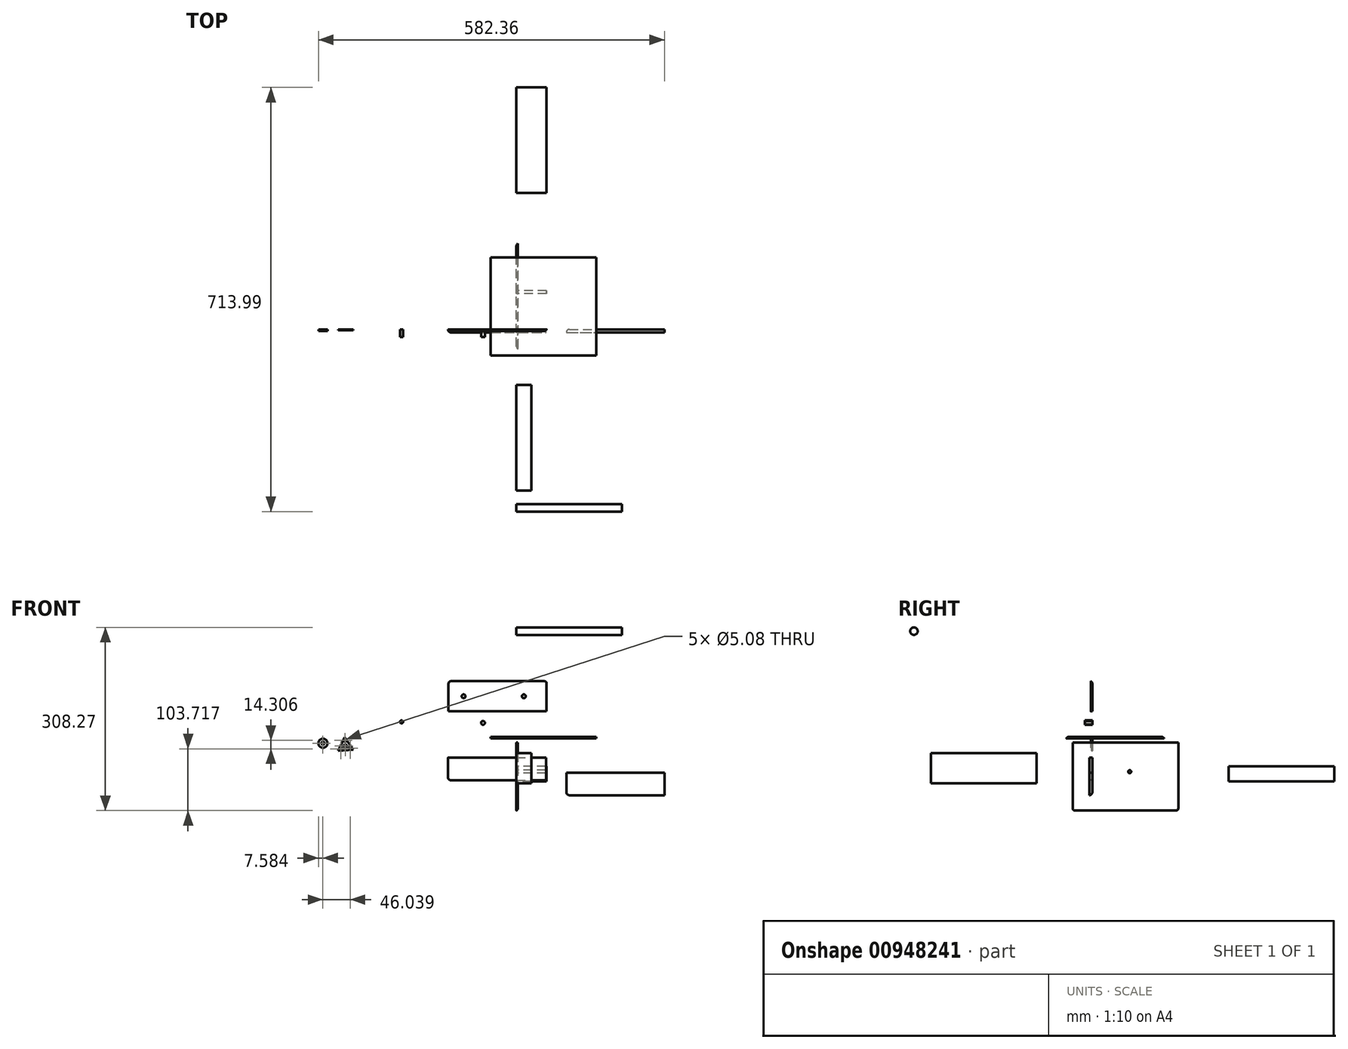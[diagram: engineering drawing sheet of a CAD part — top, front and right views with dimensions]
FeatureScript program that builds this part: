
annotation { "Feature Type Name" : "Feature", "Feature Type Description" : "" }
export const myFeature = defineFeature(function(context is Context, id is Id, definition is map)
    precondition{}
    {
        {
            var Q0;
            Q0=qCreatedBy(makeId("Top.planeOp"),FACE);
            var sketch = newSketch(context, id + "F0", { "sketchPlane" : qUnion([Q0])});
            skLineSegment(sketch, "E0.bottom", {"start": v(-43.18, -44.05) * mm, "end": v(134.62, -44.05) * mm});
            skLineSegment(sketch, "E0.top", {"start": v(-43.18, 121.05) * mm, "end": v(134.62, 121.05) * mm});
            skLineSegment(sketch, "E0.left", {"start": v(-43.18, -44.05) * mm, "end": v(-43.18, 121.05) * mm});
            skLineSegment(sketch, "E0.right", {"start": v(134.62, -44.05) * mm, "end": v(134.62, 121.05) * mm});
            skSolve(sketch);
        }
        {
            var Q0;
            Q0=makeQuery(id+"F0.imprint","IMPRINT",FACE,{"disambiguationData":[TD([[makeQuery(id+"F0.imprint","IMPRINT",EDGE,{"derivedFrom":sQuery(id+"F0.wireOp",EDGE,"E0.bottom")}),1.0]])]});
            extrude(context, id + "F1", {"entities" : qUnion([Q0]), "depth" : 2.54 * mm, "offsetDistance" : 25.4 * mm});
        }
        {
            var Q0;
            Q0=qCreatedBy(makeId("Right.planeOp"),FACE);
            var sketch = newSketch(context, id + "F2", { "sketchPlane" : qUnion([Q0])});
            skLineSegment(sketch, "E1.bottom", {"start": v(-33.12, -6.95) * mm, "end": v(144.68, -6.95) * mm});
            skLineSegment(sketch, "E1.top", {"start": v(-33.12, -121.25) * mm, "end": v(144.68, -121.25) * mm});
            skLineSegment(sketch, "E1.left", {"start": v(-33.12, -6.95) * mm, "end": v(-33.12, -121.25) * mm});
            skLineSegment(sketch, "E1.right", {"start": v(144.68, -6.95) * mm, "end": v(144.68, -121.25) * mm});
            skSolve(sketch);
        }
        {
            var Q0;
            Q0=makeQuery(id+"F2.imprint","IMPRINT",FACE,{"disambiguationData":[TD([[makeQuery(id+"F2.imprint","IMPRINT",EDGE,{"derivedFrom":sQuery(id+"F2.wireOp",EDGE,"E1.bottom")}),-1.0]])]});
            extrude(context, id + "F3", {"entities" : qUnion([Q0]), "depth" : 2.54 * mm, "offsetDistance" : 25.4 * mm});
        }
        {
            var Q0;
            Q0=qCreatedBy(makeId("Front.planeOp"),FACE);
            var sketch = newSketch(context, id + "F4", { "sketchPlane" : qUnion([Q0])});
            skLineSegment(sketch, "E2.bottom", {"start": v(-115.22, -32.41) * mm, "end": v(49.88, -32.41) * mm});
            skLineSegment(sketch, "E2.top", {"start": v(-115.22, -70.51) * mm, "end": v(49.88, -70.51) * mm});
            skLineSegment(sketch, "E2.left", {"start": v(-115.22, -32.41) * mm, "end": v(-115.22, -70.51) * mm});
            skLineSegment(sketch, "E2.right", {"start": v(49.88, -32.41) * mm, "end": v(49.88, -70.51) * mm});
            skSolve(sketch);
        }
        {
            var Q0;
            Q0=makeQuery(id+"F4.imprint","IMPRINT",FACE,{"disambiguationData":[TD([[makeQuery(id+"F4.imprint","IMPRINT",EDGE,{"derivedFrom":sQuery(id+"F4.wireOp",EDGE,"E2.bottom")}),-1.0]])]});
            extrude(context, id + "F5", {"entities" : qUnion([Q0]), "depth" : 5.08 * mm, "offsetDistance" : 25.4 * mm});
        }
        {
            var Q0;
            Q0=qCreatedBy(makeId("Right.planeOp"),FACE);
            var sketch = newSketch(context, id + "F6", { "sketchPlane" : qUnion([Q0])});
            skCircle(sketch, "E3", {"center": v(62.86, -55.9) * mm, "radius": 2.54 * mm});
            skSolve(sketch);
        }
        {
            var Q0;
            Q0=makeQuery(id+"F6.imprint","IMPRINT",FACE,{"disambiguationData":[TD([[makeQuery(id+"F6.imprint","IMPRINT",EDGE,{"derivedFrom":sQuery(id+"F6.wireOp",EDGE,"E3")}),1.0]])]});
            extrude(context, id + "F7", {"entities" : qUnion([Q0]), "depth" : 50.8 * mm, "offsetDistance" : 25.4 * mm});
        }
        {
            var Q0;
            Q0=qCreatedBy(makeId("Front.planeOp"),FACE);
            var sketch = newSketch(context, id + "F8", { "sketchPlane" : qUnion([Q0])});
            skLineSegment(sketch, "E4.bottom", {"start": v(50.77, 45.6) * mm, "end": v(-114.33, 45.6) * mm});
            skLineSegment(sketch, "E4.top", {"start": v(50.77, 96.4) * mm, "end": v(-114.33, 96.4) * mm});
            skLineSegment(sketch, "E4.left", {"start": v(50.77, 45.6) * mm, "end": v(50.77, 96.4) * mm});
            skLineSegment(sketch, "E4.right", {"start": v(-114.33, 45.6) * mm, "end": v(-114.33, 96.4) * mm});
            skSolve(sketch);
        }
        {
            var Q0;
            Q0=makeQuery(id+"F8.imprint","IMPRINT",FACE,{"disambiguationData":[TD([[makeQuery(id+"F8.imprint","IMPRINT",EDGE,{"derivedFrom":sQuery(id+"F8.wireOp",EDGE,"E4.bottom")}),-1.0]])]});
            extrude(context, id + "F9", {"entities" : qUnion([Q0]), "depth" : 2.54 * mm, "offsetDistance" : 25.4 * mm});
        }
        {
            var Q0;
            Q0=makeQuery(id+"F9.opExtrude","CAP_FACE",FACE,{"disambiguationData":[OSD([sQuery(id+"F8.wireOp",EDGE,"E4.bottom"),sQuery(id+"F8.wireOp",EDGE,"E4.top"),sQuery(id+"F8.wireOp",EDGE,"E4.left"),sQuery(id+"F8.wireOp",EDGE,"E4.right")])],"isStart":false});
            var sketch = newSketch(context, id + "F10", { "sketchPlane" : qUnion([Q0])});
            skPoint(sketch, "E5.startSnap0", {"position": v(50.77, 71) * mm});
            skLineSegment(sketch, "E6", {"start": v(50.77, 71) * mm, "end": v(-63.53, 71) * mm});
            skLineSegment(sketch, "E7", {"start": v(-63.53, 71) * mm, "end": v(-6.38, 71) * mm});
            skLineSegment(sketch, "E8", {"start": v(-63.53, 71) * mm, "end": v(-88.93, 71) * mm});
            skLineSegment(sketch, "E9", {"start": v(-88.93, 71) * mm, "end": v(-114.33, 71) * mm});
            skLineSegment(sketch, "E10", {"start": v(50.77, 71) * mm, "end": v(12.43, 71) * mm});
            skSolve(sketch);
        }
        {
            var Q0;
            Q0=sQuery(id+"F10.wireOp",VERTEX,"E10.end");
            var Q1;
            Q1=makeQuery(id+"F9.opExtrude","SWEPT_BODY",BODY,{"disambiguationData":[OSD([sQuery(id+"F8.wireOp",EDGE,"E4.bottom"),sQuery(id+"F8.wireOp",EDGE,"E4.top"),sQuery(id+"F8.wireOp",EDGE,"E4.left"),sQuery(id+"F8.wireOp",EDGE,"E4.right")])]});
            hole(context, id + "F11", {"style" : HoleStyle.SIMPLE, "endStyle" : HoleEndStyle.BLIND, "holeDiameter" : 6.35 * mm, "majorDiameter" : 6.35 * mm, "holeDepth" : 76.2 * mm, "isTappedThrough" : true, "tappedDepth" : 12.7 * mm, "tapClearance" : 3, "locations" : qUnion([Q0]), "scope" : qUnion([Q1])});
        }
        {
            var Q0;
            Q0=sQuery(id+"F10.wireOp",VERTEX,"E8.end");
            var Q1;
            Q1=makeQuery(id+"F9.opExtrude","SWEPT_BODY",BODY,{"disambiguationData":[OSD([sQuery(id+"F8.wireOp",EDGE,"E4.bottom"),sQuery(id+"F8.wireOp",EDGE,"E4.top"),sQuery(id+"F8.wireOp",EDGE,"E4.left"),sQuery(id+"F8.wireOp",EDGE,"E4.right")])]});
            hole(context, id + "F12", {"style" : HoleStyle.SIMPLE, "endStyle" : HoleEndStyle.BLIND, "holeDiameter" : 6.35 * mm, "majorDiameter" : 6.35 * mm, "holeDepth" : 76.2 * mm, "isTappedThrough" : true, "tappedDepth" : 12.7 * mm, "tapClearance" : 3, "locations" : qUnion([Q0]), "scope" : qUnion([Q1])});
        }
        {
            var Q0;
            Q0=makeQuery(id+"F3.opExtrude","CAP_EDGE",EDGE,{"disambiguationData":[OSD([sQuery(id+"F2.wireOp",EDGE,"E1.left")])],"isStart":true});
            fillet(context, id + "F13", {"entities" : qUnion([Q0]), "radius" : 5.08 * mm, "tangentPropagation" : true, "allowEdgeOverflow" : false});
        }
        {
            var Q0;
            Q0=makeQuery(id+"F3.opExtrude","CAP_EDGE",EDGE,{"disambiguationData":[OSD([sQuery(id+"F2.wireOp",EDGE,"E1.right")])],"isStart":true});
            fillet(context, id + "F14", {"entities" : qUnion([Q0]), "radius" : 5.08 * mm, "tangentPropagation" : true, "allowEdgeOverflow" : false});
        }
        {
            var Q0;
            Q0=makeQuery(id+"F3.opExtrude","CAP_EDGE",EDGE,{"disambiguationData":[OSD([sQuery(id+"F2.wireOp",EDGE,"E1.top")])],"isStart":false});
            fillet(context, id + "F15", {"entities" : qUnion([Q0]), "radius" : 5.08 * mm, "tangentPropagation" : true, "allowEdgeOverflow" : false});
        }
        {
            var Q0;
            Q0=makeQuery(id+"F1.opExtrude","CAP_EDGE",EDGE,{"disambiguationData":[OSD([sQuery(id+"F0.wireOp",EDGE,"E0.top")])],"isStart":false});
            var Q1;
            Q1=makeQuery(id+"F1.opExtrude","CAP_EDGE",EDGE,{"disambiguationData":[OSD([sQuery(id+"F0.wireOp",EDGE,"E0.bottom")])],"isStart":false});
            fillet(context, id + "F16", {"entities" : qUnion([Q0, Q1]), "radius" : 5.08 * mm, "tangentPropagation" : true, "allowEdgeOverflow" : false});
        }
        {
            var Q0;
            Q0=makeQuery(id+"F5.opExtrude","CAP_EDGE",EDGE,{"disambiguationData":[OSD([sQuery(id+"F4.wireOp",EDGE,"E2.top")])],"isStart":false});
            fillet(context, id + "F17", {"entities" : qUnion([Q0]), "radius" : 5.08 * mm, "tangentPropagation" : true, "allowEdgeOverflow" : false});
        }
        {
            var Q0;
            Q0=makeQuery(id+"F5.opExtrude","CAP_EDGE",EDGE,{"disambiguationData":[OSD([sQuery(id+"F4.wireOp",EDGE,"E2.left")])],"isStart":false});
            fillet(context, id + "F18", {"entities" : qUnion([Q0]), "radius" : 5.08 * mm, "tangentPropagation" : true, "allowEdgeOverflow" : false});
        }
        {
            var Q0;
            Q0=makeQuery(id+"F9.opExtrude","CAP_EDGE",EDGE,{"disambiguationData":[OSD([sQuery(id+"F8.wireOp",EDGE,"E4.right")])],"isStart":false});
            fillet(context, id + "F19", {"entities" : qUnion([Q0]), "radius" : 5.08 * mm, "tangentPropagation" : true, "allowEdgeOverflow" : false});
        }
        {
            var Q0;
            Q0=makeQuery(id+"F9.opExtrude","CAP_EDGE",EDGE,{"disambiguationData":[OSD([sQuery(id+"F8.wireOp",EDGE,"E4.left")])],"isStart":false});
            fillet(context, id + "F20", {"entities" : qUnion([Q0]), "radius" : 5.08 * mm, "tangentPropagation" : true, "allowEdgeOverflow" : false});
        }
        {
            var Q0;
            Q0=makeQuery(id+"F9.opExtrude","CAP_EDGE",EDGE,{"disambiguationData":[OSD([sQuery(id+"F8.wireOp",EDGE,"E4.top")])],"isStart":true});
            fillet(context, id + "F21", {"entities" : qUnion([Q0]), "radius" : 5.08 * mm, "tangentPropagation" : true, "allowEdgeOverflow" : false});
        }
        {
            var Q0;
            Q0=qCreatedBy(makeId("Front.planeOp"),FACE);
            var sketch = newSketch(context, id + "F22", { "sketchPlane" : qUnion([Q0])});
            skCircle(sketch, "E11", {"center": v(-56.3, 26.27) * mm, "radius": 3.18 * mm});
            skSolve(sketch);
        }
        {
            var Q0;
            Q0=makeQuery(id+"F22.imprint","IMPRINT",FACE,{"disambiguationData":[TD([[makeQuery(id+"F22.imprint","IMPRINT",EDGE,{"derivedFrom":sQuery(id+"F22.wireOp",EDGE,"E11")}),1.0]])]});
            extrude(context, id + "F23", {"entities" : qUnion([Q0]), "depth" : 12.7 * mm, "offsetDistance" : 25.4 * mm});
        }
        {
            var Q0;
            Q0=qCreatedBy(makeId("Front.planeOp"),FACE);
            var sketch = newSketch(context, id + "F24", { "sketchPlane" : qUnion([Q0])});
            skLineSegment(sketch, "E12", {"start": v(-289.09, 2.26) * mm, "end": v(-274.77, -18.72) * mm});
            skLineSegment(sketch, "E13", {"start": v(-274.77, -18.72) * mm, "end": v(-300.1, -20.63) * mm});
            skLineSegment(sketch, "E14", {"start": v(-300.1, -20.63) * mm, "end": v(-289.09, 2.26) * mm});
            skLineSegment(sketch, "E15", {"start": v(-288.54, -5.06) * mm, "end": v(-287.43, -19.68) * mm});
            skLineSegment(sketch, "E16", {"start": v(-294.04, -16.5) * mm, "end": v(-281.93, -8.23) * mm});
            skLineSegment(sketch, "E17", {"start": v(-281.38, -15.54) * mm, "end": v(-294.6, -9.19) * mm});
            skCircle(sketch, "E18", {"center": v(-325.73, -8.09) * mm, "radius": 7.62 * mm});
            skLineSegment(sketch, "E19", {"start": v(-294.04, -16.5) * mm, "end": v(-287.99, -12.37) * mm});
            skLineSegment(sketch, "E20", {"start": v(-288.54, -5.06) * mm, "end": v(-287.99, -12.37) * mm});
            skLineSegment(sketch, "E21", {"start": v(-281.38, -15.54) * mm, "end": v(-287.99, -12.37) * mm});
            skLineSegment(sketch, "E22", {"start": v(-287.99, -12.37) * mm, "end": v(-294.04, -16.5) * mm});
            skLineSegment(sketch, "E23", {"start": v(-281.38, -15.54) * mm, "end": v(-274.77, -18.72) * mm});
            skLineSegment(sketch, "E24", {"start": v(-274.77, -18.72) * mm, "end": v(-278.07, -17.13) * mm});
            skLineSegment(sketch, "E25", {"start": v(-288.54, -5.06) * mm, "end": v(-289.09, 2.26) * mm});
            skLineSegment(sketch, "E26", {"start": v(-300.1, -20.63) * mm, "end": v(-294.04, -16.5) * mm});
            skLineSegment(sketch, "E27", {"start": v(-294.04, -16.5) * mm, "end": v(-297.07, -18.57) * mm});
            skSolve(sketch);
        }
        {
            var Q0;
            {var subQ1=sQuery(id+"F24.wireOp",EDGE,"E14");var subQ3=sQuery(id+"F24.wireOp",EDGE,"E17");var subQ4=makeQuery(id+"F24.imprint","INTERSECT",VERTEX,{"derivedFrom":[subQ1,subQ3]});Q0=makeQuery(id+"F24.imprint","IMPRINT",FACE,{"disambiguationData":[TD([[makeQuery(id+"F24.imprint","IMPRINT",EDGE,{"disambiguationData":[TD([[subQ4,-1.0]])],"derivedFrom":subQ1}),-1.0]])]});}
            var Q1;
            {var subQ1=sQuery(id+"F24.wireOp",EDGE,"E12");var subQ3=sQuery(id+"F24.wireOp",EDGE,"E16");var subQ4=makeQuery(id+"F24.imprint","INTERSECT",VERTEX,{"derivedFrom":[subQ1,subQ3]});Q1=makeQuery(id+"F24.imprint","IMPRINT",FACE,{"disambiguationData":[TD([[makeQuery(id+"F24.imprint","IMPRINT",EDGE,{"disambiguationData":[TD([[subQ4,1.0]])],"derivedFrom":subQ1}),-1.0]])]});}
            var Q2;
            {var subQ1=sQuery(id+"F24.wireOp",EDGE,"E14");var subQ3=sQuery(id+"F24.wireOp",EDGE,"E17");var subQ4=makeQuery(id+"F24.imprint","INTERSECT",VERTEX,{"derivedFrom":[subQ1,subQ3]});Q2=makeQuery(id+"F24.imprint","IMPRINT",FACE,{"disambiguationData":[TD([[makeQuery(id+"F24.imprint","IMPRINT",EDGE,{"disambiguationData":[TD([[subQ4,1.0]])],"derivedFrom":subQ1}),-1.0]])]});}
            var Q3;
            {var subQ1=sQuery(id+"F24.wireOp",EDGE,"E13");var subQ3=sQuery(id+"F24.wireOp",EDGE,"E15");var subQ4=makeQuery(id+"F24.imprint","INTERSECT",VERTEX,{"derivedFrom":[subQ1,subQ3]});Q3=makeQuery(id+"F24.imprint","IMPRINT",FACE,{"disambiguationData":[TD([[makeQuery(id+"F24.imprint","IMPRINT",EDGE,{"disambiguationData":[TD([[subQ4,-1.0]])],"derivedFrom":subQ1}),-1.0]])]});}
            var Q4;
            {var subQ1=sQuery(id+"F24.wireOp",EDGE,"E12");var subQ3=sQuery(id+"F24.wireOp",EDGE,"E16");var subQ4=makeQuery(id+"F24.imprint","INTERSECT",VERTEX,{"derivedFrom":[subQ1,subQ3]});Q4=makeQuery(id+"F24.imprint","IMPRINT",FACE,{"disambiguationData":[TD([[makeQuery(id+"F24.imprint","IMPRINT",EDGE,{"disambiguationData":[TD([[subQ4,-1.0]])],"derivedFrom":subQ1}),-1.0]])]});}
            var Q5;
            {var subQ1=sQuery(id+"F24.wireOp",EDGE,"E13");var subQ3=sQuery(id+"F24.wireOp",EDGE,"E15");var subQ4=makeQuery(id+"F24.imprint","INTERSECT",VERTEX,{"derivedFrom":[subQ1,subQ3]});Q5=makeQuery(id+"F24.imprint","IMPRINT",FACE,{"disambiguationData":[TD([[makeQuery(id+"F24.imprint","IMPRINT",EDGE,{"disambiguationData":[TD([[subQ4,1.0]])],"derivedFrom":subQ1}),-1.0]])]});}
            var Q6;
            Q6=makeQuery(id+"F24.imprint","IMPRINT",FACE,{"disambiguationData":[TD([[makeQuery(id+"F24.imprint","IMPRINT",EDGE,{"derivedFrom":sQuery(id+"F24.wireOp",EDGE,"E18")}),1.0]])]});
            extrude(context, id + "F25", {"entities" : qUnion([Q0, Q1, Q2, Q3, Q4, Q5, Q6]), "depth" : 1.27 * mm, "offsetDistance" : 25.4 * mm});
        }
        {
            var Q0;
            Q0=makeQuery(id+"F25.opExtrude","CAP_FACE",FACE,{"disambiguationData":[OSD([sQuery(id+"F24.wireOp",EDGE,"E18")])],"isStart":false});
            extrude(context, id + "F26", {"entities" : qUnion([Q0]), "operationType" : NewBodyOperationType.ADD, "depth" : 1.27 * mm, "offsetDistance" : 25.4 * mm});
        }
        {
            var Q0;
            Q0=makeQuery(id+"F25.opExtrude","CAP_FACE",FACE,{"disambiguationData":[OSD([sQuery(id+"F24.wireOp",EDGE,"E12"),sQuery(id+"F24.wireOp",EDGE,"E13"),sQuery(id+"F24.wireOp",EDGE,"E14")])],"isStart":false});
            var sketch = newSketch(context, id + "F27", { "sketchPlane" : qUnion([Q0])});
            skLineSegment(sketch, "E28", {"start": v(-289.09, 2.26) * mm, "end": v(-287.43, -19.68) * mm});
            skLineSegment(sketch, "E29", {"start": v(-274.77, -18.72) * mm, "end": v(-294.6, -9.19) * mm});
            skLineSegment(sketch, "E30", {"start": v(-300.1, -20.63) * mm, "end": v(-281.93, -8.23) * mm});
            skLineSegment(sketch, "E31", {"start": v(-274.77, -18.72) * mm, "end": v(-284.68, -13.96) * mm});
            skLineSegment(sketch, "E32", {"start": v(-300.1, -20.63) * mm, "end": v(-291.01, -14.43) * mm});
            skLineSegment(sketch, "E33", {"start": v(-289.09, 2.26) * mm, "end": v(-288.26, -8.71) * mm});
            skLineSegment(sketch, "E34", {"start": v(-288.26, -8.71) * mm, "end": v(-288.68, -3.23) * mm});
            skLineSegment(sketch, "E35", {"start": v(-274.77, -18.72) * mm, "end": v(-279.73, -16.34) * mm});
            skLineSegment(sketch, "E36", {"start": v(-300.1, -20.63) * mm, "end": v(-295.56, -17.53) * mm});
            skLineSegment(sketch, "E37", {"start": v(-295.56, -17.53) * mm, "end": v(-297.83, -19.08) * mm});
            skLineSegment(sketch, "E38", {"start": v(-274.77, -18.72) * mm, "end": v(-277.25, -17.53) * mm});
            skLineSegment(sketch, "E39", {"start": v(-288.68, -3.23) * mm, "end": v(-288.92, 0) * mm});
            skLineSegment(sketch, "E40", {"start": v(-288.26, -8.71) * mm, "end": v(-288.47, -5.97) * mm});
            skLineSegment(sketch, "E41", {"start": v(-291.01, -14.43) * mm, "end": v(-293.3, -15.99) * mm});
            skLineSegment(sketch, "E42", {"start": v(-284.68, -13.96) * mm, "end": v(-281.93, -15.28) * mm});
            skLineSegment(sketch, "E43", {"start": v(-291.01, -14.43) * mm, "end": v(-287.99, -12.37) * mm});
            skSolve(sketch);
        }
        {
            var Q0;
            Q0=sQuery(id+"F27.wireOp",VERTEX,"E34.end");
            var Q1;
            Q1=sQuery(id+"F27.wireOp",VERTEX,"E36.end");
            var Q2;
            Q2=sQuery(id+"F27.wireOp",VERTEX,"E35.end");
            var Q3;
            Q3=sQuery(id+"F27.wireOp",VERTEX,"E43.end");
            var Q4;
            Q4=makeQuery(id+"F25.opExtrude","SWEPT_BODY",BODY,{"disambiguationData":[OSD([sQuery(id+"F24.wireOp",EDGE,"E12"),sQuery(id+"F24.wireOp",EDGE,"E13"),sQuery(id+"F24.wireOp",EDGE,"E14")])]});
            hole(context, id + "F28", {"style" : HoleStyle.SIMPLE, "endStyle" : HoleEndStyle.BLIND, "holeDiameter" : 5.08 * mm, "majorDiameter" : 6.35 * mm, "holeDepth" : 76.2 * mm, "isTappedThrough" : true, "tappedDepth" : 12.7 * mm, "tapClearance" : 3, "locations" : qUnion([Q0, Q1, Q2, Q3]), "scope" : qUnion([Q4])});
        }
        {
            var Q0;
            Q0=makeQuery(id+"F26.opExtrude","CAP_FACE",FACE,{"disambiguationData":[OSD([sQuery(id+"F24.wireOp",EDGE,"E18")])],"isStart":false});
            var sketch = newSketch(context, id + "F29", { "sketchPlane" : qUnion([Q0])});
            skLineSegment(sketch, "E44", {"start": v(-318.31, -6.35) * mm, "end": v(-333.22, -9.52) * mm});
            skLineSegment(sketch, "E45", {"start": v(-333.22, -9.52) * mm, "end": v(-325.77, -7.94) * mm});
            skLineSegment(sketch, "E46", {"start": v(-325.77, -7.94) * mm, "end": v(-327.32, -0.63) * mm});
            skLineSegment(sketch, "E47", {"start": v(-327.32, -0.63) * mm, "end": v(-324.15, -15.54) * mm});
            skSolve(sketch);
        }
        {
            var Q0;
            Q0=sQuery(id+"F29.wireOp",VERTEX,"E45.end");
            var Q1;
            Q1=makeQuery(id+"F25.opExtrude","SWEPT_BODY",BODY,{"disambiguationData":[OSD([sQuery(id+"F24.wireOp",EDGE,"E18")])]});
            hole(context, id + "F30", {"style" : HoleStyle.SIMPLE, "endStyle" : HoleEndStyle.BLIND, "holeDiameter" : 5.08 * mm, "majorDiameter" : 6.35 * mm, "holeDepth" : 76.2 * mm, "isTappedThrough" : true, "tappedDepth" : 12.7 * mm, "tapClearance" : 3, "locations" : qUnion([Q0]), "scope" : qUnion([Q1])});
        }
        {
            var Q0;
            Q0=qCreatedBy(makeId("Front.planeOp"),FACE);
            var sketch = newSketch(context, id + "F31", { "sketchPlane" : qUnion([Q0])});
            skCircle(sketch, "E48", {"center": v(-193.41, 27.84) * mm, "radius": 2.54 * mm});
            skSolve(sketch);
        }
        {
            var Q0;
            Q0=makeQuery(id+"F31.imprint","IMPRINT",FACE,{"disambiguationData":[TD([[makeQuery(id+"F31.imprint","IMPRINT",EDGE,{"derivedFrom":sQuery(id+"F31.wireOp",EDGE,"E48")}),1.0]])]});
            extrude(context, id + "F32", {"entities" : qUnion([Q0]), "depth" : 12.7 * mm, "offsetDistance" : 25.4 * mm});
        }
        {
            var Q0;
            Q0=qCreatedBy(makeId("Right.planeOp"),FACE);
            var sketch = newSketch(context, id + "F33", { "sketchPlane" : qUnion([Q0])});
            skLineSegment(sketch, "E49.bottom", {"start": v(-93.7, -75.62) * mm, "end": v(-271.5, -75.62) * mm});
            skLineSegment(sketch, "E49.top", {"start": v(-93.7, -24.82) * mm, "end": v(-271.5, -24.82) * mm});
            skLineSegment(sketch, "E49.left", {"start": v(-93.7, -75.62) * mm, "end": v(-93.7, -24.82) * mm});
            skLineSegment(sketch, "E49.right", {"start": v(-271.5, -75.62) * mm, "end": v(-271.5, -24.82) * mm});
            skSolve(sketch);
        }
        {
            var Q0;
            Q0=makeQuery(id+"F33.imprint","IMPRINT",FACE,{"disambiguationData":[TD([[makeQuery(id+"F33.imprint","IMPRINT",EDGE,{"derivedFrom":sQuery(id+"F33.wireOp",EDGE,"E49.bottom")}),-1.0]])]});
            extrude(context, id + "F34", {"entities" : qUnion([Q0]), "depth" : 25.4 * mm, "offsetDistance" : 25.4 * mm});
        }
        {
            var Q0;
            Q0=qCreatedBy(makeId("Front.planeOp"),FACE);
            var sketch = newSketch(context, id + "F35", { "sketchPlane" : qUnion([Q0])});
            skLineSegment(sketch, "E50.bottom", {"start": v(83.9, -95.52) * mm, "end": v(249, -95.52) * mm});
            skLineSegment(sketch, "E50.top", {"start": v(83.9, -57.42) * mm, "end": v(249, -57.42) * mm});
            skLineSegment(sketch, "E50.left", {"start": v(83.9, -95.52) * mm, "end": v(83.9, -57.42) * mm});
            skLineSegment(sketch, "E50.right", {"start": v(249, -95.52) * mm, "end": v(249, -57.42) * mm});
            skSolve(sketch);
        }
        {
            var Q0;
            Q0=makeQuery(id+"F35.imprint","IMPRINT",FACE,{"disambiguationData":[TD([[makeQuery(id+"F35.imprint","IMPRINT",EDGE,{"derivedFrom":sQuery(id+"F35.wireOp",EDGE,"E50.bottom")}),1.0]])]});
            extrude(context, id + "F36", {"entities" : qUnion([Q0]), "depth" : 5.08 * mm, "offsetDistance" : 25.4 * mm});
        }
        {
            var Q0;
            Q0=makeQuery(id+"F36.opExtrude","CAP_EDGE",EDGE,{"disambiguationData":[OSD([sQuery(id+"F35.wireOp",EDGE,"E50.left")])],"isStart":true});
            var Q1;
            Q1=makeQuery(id+"F36.opExtrude","CAP_EDGE",EDGE,{"disambiguationData":[OSD([sQuery(id+"F35.wireOp",EDGE,"E50.bottom")])],"isStart":true});
            fillet(context, id + "F37", {"entities" : qUnion([Q0, Q1]), "radius" : 5.08 * mm, "tangentPropagation" : true, "allowEdgeOverflow" : false});
        }
        {
            var Q0;
            Q0=makeQuery(id+"F37.opFillet","BLEND_EDGE",EDGE,{"blendedFrom":[makeQuery(id+"F36.opExtrude","CAP_EDGE",EDGE,{"disambiguationData":[OSD([sQuery(id+"F35.wireOp",EDGE,"E50.bottom")])],"isStart":true}),makeQuery(id+"F36.opExtrude","CAP_EDGE",EDGE,{"disambiguationData":[OSD([sQuery(id+"F35.wireOp",EDGE,"E50.left")])],"isStart":true})],"blendedInto":[]});
            fillet(context, id + "F38", {"entities" : qUnion([Q0]), "radius" : 5.08 * mm, "tangentPropagation" : true, "allowEdgeOverflow" : false});
        }
        {
            var Q0;
            Q0=qCreatedBy(makeId("Right.planeOp"),FACE);
            var sketch = newSketch(context, id + "F39", { "sketchPlane" : qUnion([Q0])});
            skLineSegment(sketch, "E51.bottom", {"start": v(229.6, -47.14) * mm, "end": v(407.4, -47.14) * mm});
            skLineSegment(sketch, "E51.top", {"start": v(229.6, -72.54) * mm, "end": v(407.4, -72.54) * mm});
            skLineSegment(sketch, "E51.left", {"start": v(229.6, -47.14) * mm, "end": v(229.6, -72.54) * mm});
            skLineSegment(sketch, "E51.right", {"start": v(407.4, -47.14) * mm, "end": v(407.4, -72.54) * mm});
            skSolve(sketch);
        }
        {
            var Q0;
            Q0=makeQuery(id+"F39.imprint","IMPRINT",FACE,{"disambiguationData":[TD([[makeQuery(id+"F39.imprint","IMPRINT",EDGE,{"derivedFrom":sQuery(id+"F39.wireOp",EDGE,"E51.bottom")}),-1.0]])]});
            extrude(context, id + "F40", {"entities" : qUnion([Q0]), "depth" : 50.8 * mm, "offsetDistance" : 25.4 * mm});
        }
        {
            var Q0;
            Q0=qCreatedBy(makeId("Right.planeOp"),FACE);
            var sketch = newSketch(context, id + "F41", { "sketchPlane" : qUnion([Q0])});
            skCircle(sketch, "E52", {"center": v(-300.24, 180.67) * mm, "radius": 6.35 * mm});
            skSolve(sketch);
        }
        {
            var Q0;
            Q0=makeQuery(id+"F41.imprint","IMPRINT",FACE,{"disambiguationData":[TD([[makeQuery(id+"F41.imprint","IMPRINT",EDGE,{"derivedFrom":sQuery(id+"F41.wireOp",EDGE,"E52")}),1.0]])]});
            extrude(context, id + "F42", {"entities" : qUnion([Q0]), "depth" : 177.8 * mm, "offsetDistance" : 25.4 * mm});
        }
    });
